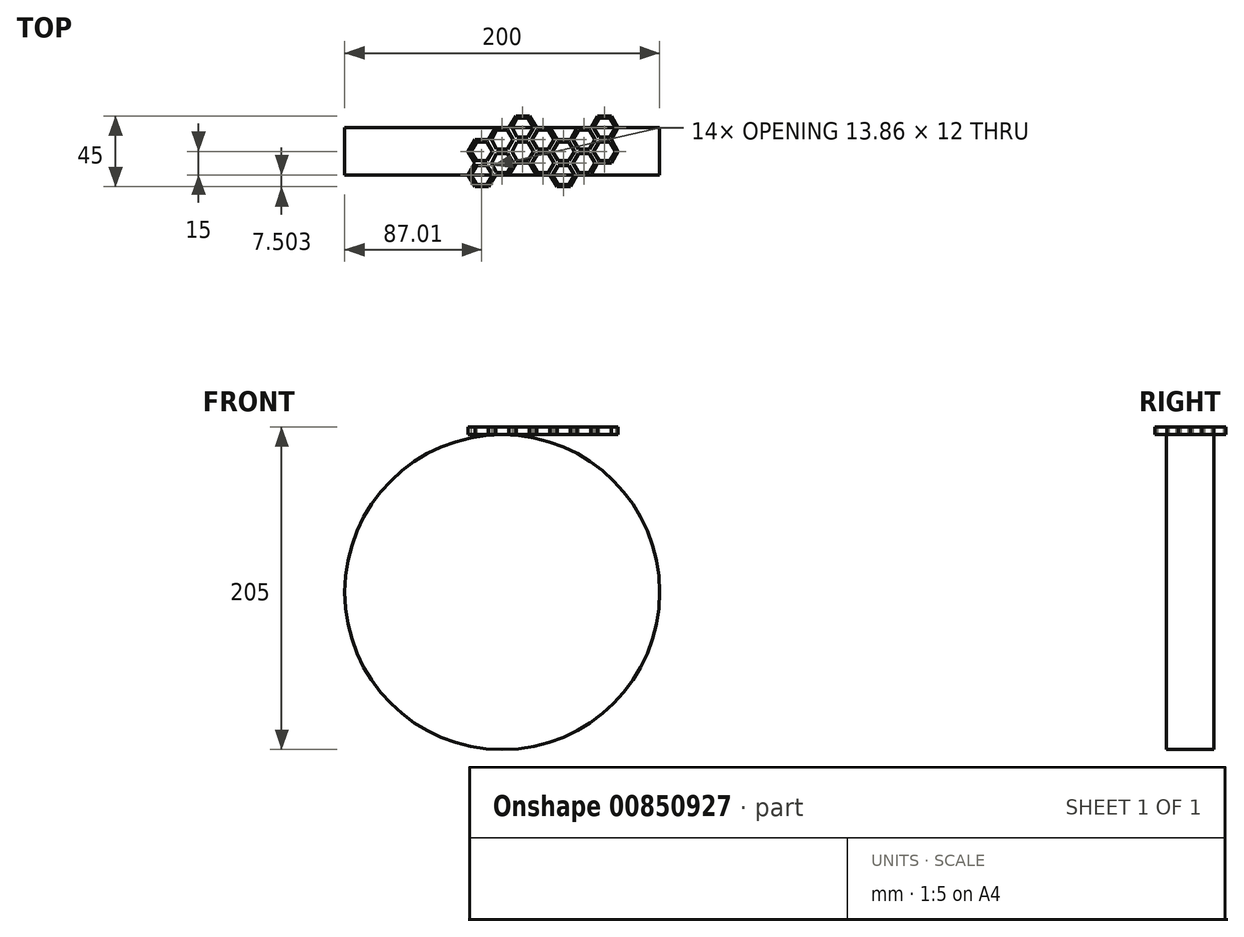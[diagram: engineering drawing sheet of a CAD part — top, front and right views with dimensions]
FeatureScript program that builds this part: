
annotation { "Feature Type Name" : "Feature", "Feature Type Description" : "" }
export const myFeature = defineFeature(function(context is Context, id is Id, definition is map)
    precondition{}
    {
        {
            var Q0;
            Q0=qCreatedBy(makeId("Front.planeOp"),FACE);
            var sketch = newSketch(context, id + "F0", { "sketchPlane" : qUnion([Q0])});
            skCircle(sketch, "E0", {"center": v(0, 0) * mm, "radius": 100 * mm});
            skSolve(sketch);
        }
        {
            var Q0;
            Q0=makeQuery(id+"F0.imprint","IMPRINT",FACE,{"disambiguationData":[TD([[makeQuery(id+"F0.imprint","IMPRINT",EDGE,{"derivedFrom":sQuery(id+"F0.wireOp",EDGE,"E0")}),1.0]])]});
            extrude(context, id + "F1", {"entities" : qUnion([Q0]), "depth" : 30 * mm, "offsetDistance" : 25 * mm});
        }
        {
            var Q0;
            Q0=qCreatedBy(makeId("Top.planeOp"),FACE);
            cPlane(context, id + "F2", {"entities" : qUnion([Q0]), "cplaneType" : CPlaneType.OFFSET, "offset" : 100 * mm, "width" : 150 * mm, "height" : 150 * mm});
        }
        {
            var Q0;
            Q0=qCreatedBy(id+"F2.planeOp",FACE);
            var sketch = newSketch(context, id + "F3", { "sketchPlane" : qUnion([Q0])});
            skCircle(sketch, "E1.cCircle", {"center": v(0, -7.45) * mm, "radius": 7.5 * mm, "construction": true});
            skLineSegment(sketch, "E1.0", {"start": v(4.33, -14.95) * mm, "end": v(-4.33, -14.95) * mm});
            skLineSegment(sketch, "E1.1", {"start": v(-4.33, -14.95) * mm, "end": v(-8.66, -7.45) * mm});
            skLineSegment(sketch, "E1.2", {"start": v(-8.66, -7.45) * mm, "end": v(-4.33, 0.05) * mm});
            skLineSegment(sketch, "E1.3", {"start": v(-4.33, 0.05) * mm, "end": v(4.33, 0.05) * mm});
            skLineSegment(sketch, "E1.4", {"start": v(4.33, 0.05) * mm, "end": v(8.66, -7.45) * mm});
            skLineSegment(sketch, "E1.5", {"start": v(8.66, -7.45) * mm, "end": v(4.33, -14.95) * mm});
            skPoint(sketch, "E1.0.midPoint", {"position": v(0, -14.95) * mm});
            skCircle(sketch, "E2.cCircle", {"center": v(0, -7.45) * mm, "radius": 6 * mm, "construction": true});
            skLineSegment(sketch, "E2.0", {"start": v(3.46, -13.45) * mm, "end": v(-3.46, -13.45) * mm});
            skLineSegment(sketch, "E2.1", {"start": v(-3.46, -13.45) * mm, "end": v(-6.93, -7.45) * mm});
            skLineSegment(sketch, "E2.2", {"start": v(-6.93, -7.45) * mm, "end": v(-3.46, -1.45) * mm});
            skLineSegment(sketch, "E2.3", {"start": v(-3.46, -1.45) * mm, "end": v(3.46, -1.45) * mm});
            skLineSegment(sketch, "E2.4", {"start": v(3.46, -1.45) * mm, "end": v(6.93, -7.45) * mm});
            skLineSegment(sketch, "E2.5", {"start": v(6.93, -7.45) * mm, "end": v(3.46, -13.45) * mm});
            skPoint(sketch, "E2.0.midPoint", {"position": v(0, -13.45) * mm});
            skCircle(sketch, "E3.cCircle", {"center": v(0, -22.45) * mm, "radius": 7.5 * mm, "construction": true});
            skLineSegment(sketch, "E3.0", {"start": v(4.33, -29.95) * mm, "end": v(-4.33, -29.95) * mm});
            skLineSegment(sketch, "E3.1", {"start": v(-4.33, -29.95) * mm, "end": v(-8.66, -22.45) * mm});
            skLineSegment(sketch, "E3.2", {"start": v(-8.66, -22.45) * mm, "end": v(-4.33, -14.95) * mm});
            skLineSegment(sketch, "E3.3", {"start": v(-4.33, -14.95) * mm, "end": v(4.33, -14.95) * mm});
            skLineSegment(sketch, "E3.4", {"start": v(4.33, -14.95) * mm, "end": v(8.66, -22.45) * mm});
            skLineSegment(sketch, "E3.5", {"start": v(8.66, -22.45) * mm, "end": v(4.33, -29.95) * mm});
            skPoint(sketch, "E3.0.midPoint", {"position": v(0, -29.95) * mm});
            skCircle(sketch, "E4.cCircle", {"center": v(0, -22.45) * mm, "radius": 6 * mm, "construction": true});
            skLineSegment(sketch, "E4.0", {"start": v(3.46, -28.45) * mm, "end": v(-3.46, -28.45) * mm});
            skLineSegment(sketch, "E4.1", {"start": v(-3.46, -28.45) * mm, "end": v(-6.93, -22.45) * mm});
            skLineSegment(sketch, "E4.2", {"start": v(-6.93, -22.45) * mm, "end": v(-3.46, -16.45) * mm});
            skLineSegment(sketch, "E4.3", {"start": v(-3.46, -16.45) * mm, "end": v(3.46, -16.45) * mm});
            skLineSegment(sketch, "E4.4", {"start": v(3.46, -16.45) * mm, "end": v(6.93, -22.45) * mm});
            skLineSegment(sketch, "E4.5", {"start": v(6.93, -22.45) * mm, "end": v(3.46, -28.45) * mm});
            skPoint(sketch, "E4.0.midPoint", {"position": v(0, -28.45) * mm});
            skCircle(sketch, "E5.cCircle", {"center": v(13, -14.95) * mm, "radius": 7.5 * mm, "construction": true});
            skLineSegment(sketch, "E5.0", {"start": v(17.32, -22.45) * mm, "end": v(8.66, -22.45) * mm});
            skLineSegment(sketch, "E5.1", {"start": v(8.66, -22.45) * mm, "end": v(4.33, -14.95) * mm});
            skLineSegment(sketch, "E5.2", {"start": v(4.33, -14.95) * mm, "end": v(8.66, -7.45) * mm});
            skLineSegment(sketch, "E5.3", {"start": v(8.66, -7.45) * mm, "end": v(17.32, -7.45) * mm});
            skLineSegment(sketch, "E5.4", {"start": v(17.32, -7.45) * mm, "end": v(21.65, -14.95) * mm});
            skLineSegment(sketch, "E5.5", {"start": v(21.65, -14.95) * mm, "end": v(17.32, -22.45) * mm});
            skPoint(sketch, "E5.0.midPoint", {"position": v(13, -22.45) * mm});
            skCircle(sketch, "E6.cCircle", {"center": v(13, -14.95) * mm, "radius": 6 * mm, "construction": true});
            skLineSegment(sketch, "E6.0", {"start": v(16.45, -20.95) * mm, "end": v(9.53, -20.95) * mm});
            skLineSegment(sketch, "E6.1", {"start": v(9.53, -20.95) * mm, "end": v(6.06, -14.95) * mm});
            skLineSegment(sketch, "E6.2", {"start": v(6.06, -14.95) * mm, "end": v(9.53, -8.95) * mm});
            skLineSegment(sketch, "E6.3", {"start": v(9.53, -8.95) * mm, "end": v(16.45, -8.95) * mm});
            skLineSegment(sketch, "E6.4", {"start": v(16.45, -8.95) * mm, "end": v(19.92, -14.95) * mm});
            skLineSegment(sketch, "E6.5", {"start": v(19.92, -14.95) * mm, "end": v(16.45, -20.95) * mm});
            skPoint(sketch, "E6.0.midPoint", {"position": v(13, -20.95) * mm});
            skCircle(sketch, "E7.cCircle", {"center": v(13, 0.05) * mm, "radius": 7.5 * mm, "construction": true});
            skLineSegment(sketch, "E7.0", {"start": v(17.32, -7.45) * mm, "end": v(8.66, -7.45) * mm});
            skLineSegment(sketch, "E7.1", {"start": v(8.66, -7.45) * mm, "end": v(4.33, 0.05) * mm});
            skLineSegment(sketch, "E7.2", {"start": v(4.33, 0.05) * mm, "end": v(8.66, 7.55) * mm});
            skLineSegment(sketch, "E7.3", {"start": v(8.66, 7.55) * mm, "end": v(17.32, 7.55) * mm});
            skLineSegment(sketch, "E7.4", {"start": v(17.32, 7.55) * mm, "end": v(21.65, 0.05) * mm});
            skLineSegment(sketch, "E7.5", {"start": v(21.65, 0.05) * mm, "end": v(17.32, -7.45) * mm});
            skPoint(sketch, "E7.0.midPoint", {"position": v(13, -7.45) * mm});
            skCircle(sketch, "E8.cCircle", {"center": v(13, 0.05) * mm, "radius": 6 * mm, "construction": true});
            skLineSegment(sketch, "E8.0", {"start": v(16.45, -5.95) * mm, "end": v(9.53, -5.95) * mm});
            skLineSegment(sketch, "E8.1", {"start": v(9.53, -5.95) * mm, "end": v(6.06, 0.05) * mm});
            skLineSegment(sketch, "E8.2", {"start": v(6.06, 0.05) * mm, "end": v(9.53, 6.05) * mm});
            skLineSegment(sketch, "E8.3", {"start": v(9.53, 6.05) * mm, "end": v(16.45, 6.05) * mm});
            skLineSegment(sketch, "E8.4", {"start": v(16.45, 6.05) * mm, "end": v(19.92, 0.05) * mm});
            skLineSegment(sketch, "E8.5", {"start": v(19.92, 0.05) * mm, "end": v(16.45, -5.95) * mm});
            skPoint(sketch, "E8.0.midPoint", {"position": v(13, -5.95) * mm});
            skCircle(sketch, "E9.cCircle", {"center": v(25.98, -7.45) * mm, "radius": 7.5 * mm, "construction": true});
            skLineSegment(sketch, "E9.0", {"start": v(30.31, -14.95) * mm, "end": v(21.65, -14.95) * mm});
            skLineSegment(sketch, "E9.1", {"start": v(21.65, -14.95) * mm, "end": v(17.32, -7.45) * mm});
            skLineSegment(sketch, "E9.2", {"start": v(17.32, -7.45) * mm, "end": v(21.65, 0.05) * mm});
            skLineSegment(sketch, "E9.3", {"start": v(21.65, 0.05) * mm, "end": v(30.31, 0.05) * mm});
            skLineSegment(sketch, "E9.4", {"start": v(30.31, 0.05) * mm, "end": v(34.64, -7.45) * mm});
            skLineSegment(sketch, "E9.5", {"start": v(34.64, -7.45) * mm, "end": v(30.31, -14.95) * mm});
            skPoint(sketch, "E9.0.midPoint", {"position": v(25.98, -14.95) * mm});
            skCircle(sketch, "E10.cCircle", {"center": v(25.98, -7.45) * mm, "radius": 6 * mm, "construction": true});
            skLineSegment(sketch, "E10.0", {"start": v(29.44, -13.45) * mm, "end": v(22.52, -13.45) * mm});
            skLineSegment(sketch, "E10.1", {"start": v(22.52, -13.45) * mm, "end": v(19.05, -7.45) * mm});
            skLineSegment(sketch, "E10.2", {"start": v(19.05, -7.45) * mm, "end": v(22.52, -1.45) * mm});
            skLineSegment(sketch, "E10.3", {"start": v(22.52, -1.45) * mm, "end": v(29.44, -1.45) * mm});
            skLineSegment(sketch, "E10.4", {"start": v(29.44, -1.45) * mm, "end": v(32.9, -7.45) * mm});
            skLineSegment(sketch, "E10.5", {"start": v(32.9, -7.45) * mm, "end": v(29.44, -13.45) * mm});
            skPoint(sketch, "E10.0.midPoint", {"position": v(25.98, -13.45) * mm});
            skCircle(sketch, "E11.cCircle", {"center": v(25.98, -22.45) * mm, "radius": 7.5 * mm, "construction": true});
            skLineSegment(sketch, "E11.0", {"start": v(30.31, -29.95) * mm, "end": v(21.65, -29.95) * mm});
            skLineSegment(sketch, "E11.1", {"start": v(21.65, -29.95) * mm, "end": v(17.32, -22.45) * mm});
            skLineSegment(sketch, "E11.2", {"start": v(17.32, -22.45) * mm, "end": v(21.65, -14.95) * mm});
            skLineSegment(sketch, "E11.3", {"start": v(21.65, -14.95) * mm, "end": v(30.31, -14.95) * mm});
            skLineSegment(sketch, "E11.4", {"start": v(30.31, -14.95) * mm, "end": v(34.64, -22.45) * mm});
            skLineSegment(sketch, "E11.5", {"start": v(34.64, -22.45) * mm, "end": v(30.31, -29.95) * mm});
            skPoint(sketch, "E11.0.midPoint", {"position": v(25.98, -29.95) * mm});
            skCircle(sketch, "E12.cCircle", {"center": v(25.98, -22.45) * mm, "radius": 6 * mm, "construction": true});
            skLineSegment(sketch, "E12.0", {"start": v(29.44, -28.45) * mm, "end": v(22.52, -28.45) * mm});
            skLineSegment(sketch, "E12.1", {"start": v(22.52, -28.45) * mm, "end": v(19.05, -22.45) * mm});
            skLineSegment(sketch, "E12.2", {"start": v(19.05, -22.45) * mm, "end": v(22.52, -16.45) * mm});
            skLineSegment(sketch, "E12.3", {"start": v(22.52, -16.45) * mm, "end": v(29.44, -16.45) * mm});
            skLineSegment(sketch, "E12.4", {"start": v(29.44, -16.45) * mm, "end": v(32.9, -22.45) * mm});
            skLineSegment(sketch, "E12.5", {"start": v(32.9, -22.45) * mm, "end": v(29.44, -28.45) * mm});
            skPoint(sketch, "E12.0.midPoint", {"position": v(25.98, -28.45) * mm});
            skCircle(sketch, "E13.cCircle", {"center": v(38.97, -29.95) * mm, "radius": 7.5 * mm, "construction": true});
            skLineSegment(sketch, "E13.0", {"start": v(43.3, -37.45) * mm, "end": v(34.64, -37.45) * mm});
            skLineSegment(sketch, "E13.1", {"start": v(34.64, -37.45) * mm, "end": v(30.31, -29.95) * mm});
            skLineSegment(sketch, "E13.2", {"start": v(30.31, -29.95) * mm, "end": v(34.64, -22.45) * mm});
            skLineSegment(sketch, "E13.3", {"start": v(34.64, -22.45) * mm, "end": v(43.3, -22.45) * mm});
            skLineSegment(sketch, "E13.4", {"start": v(43.3, -22.45) * mm, "end": v(47.63, -29.95) * mm});
            skLineSegment(sketch, "E13.5", {"start": v(47.63, -29.95) * mm, "end": v(43.3, -37.45) * mm});
            skPoint(sketch, "E13.0.midPoint", {"position": v(38.97, -37.45) * mm});
            skCircle(sketch, "E14.cCircle", {"center": v(38.97, -29.95) * mm, "radius": 6 * mm, "construction": true});
            skLineSegment(sketch, "E14.0", {"start": v(42.44, -35.95) * mm, "end": v(35.5, -35.95) * mm});
            skLineSegment(sketch, "E14.1", {"start": v(35.5, -35.95) * mm, "end": v(32.04, -29.95) * mm});
            skLineSegment(sketch, "E14.2", {"start": v(32.04, -29.95) * mm, "end": v(35.5, -23.95) * mm});
            skLineSegment(sketch, "E14.3", {"start": v(35.5, -23.95) * mm, "end": v(42.44, -23.95) * mm});
            skLineSegment(sketch, "E14.4", {"start": v(42.44, -23.95) * mm, "end": v(45.9, -29.95) * mm});
            skLineSegment(sketch, "E14.5", {"start": v(45.9, -29.95) * mm, "end": v(42.44, -35.95) * mm});
            skPoint(sketch, "E14.0.midPoint", {"position": v(38.97, -35.95) * mm});
            skCircle(sketch, "E15.cCircle", {"center": v(38.97, -14.95) * mm, "radius": 7.5 * mm, "construction": true});
            skLineSegment(sketch, "E15.0", {"start": v(43.3, -22.45) * mm, "end": v(34.64, -22.45) * mm});
            skLineSegment(sketch, "E15.1", {"start": v(34.64, -22.45) * mm, "end": v(30.31, -14.95) * mm});
            skLineSegment(sketch, "E15.2", {"start": v(30.31, -14.95) * mm, "end": v(34.64, -7.45) * mm});
            skLineSegment(sketch, "E15.3", {"start": v(34.64, -7.45) * mm, "end": v(43.3, -7.45) * mm});
            skLineSegment(sketch, "E15.4", {"start": v(43.3, -7.45) * mm, "end": v(47.63, -14.95) * mm});
            skLineSegment(sketch, "E15.5", {"start": v(47.63, -14.95) * mm, "end": v(43.3, -22.45) * mm});
            skPoint(sketch, "E15.0.midPoint", {"position": v(38.97, -22.45) * mm});
            skCircle(sketch, "E16.cCircle", {"center": v(38.97, -14.95) * mm, "radius": 6 * mm, "construction": true});
            skLineSegment(sketch, "E16.0", {"start": v(42.44, -20.95) * mm, "end": v(35.5, -20.95) * mm});
            skLineSegment(sketch, "E16.1", {"start": v(35.5, -20.95) * mm, "end": v(32.04, -14.95) * mm});
            skLineSegment(sketch, "E16.2", {"start": v(32.04, -14.95) * mm, "end": v(35.5, -8.95) * mm});
            skLineSegment(sketch, "E16.3", {"start": v(35.5, -8.95) * mm, "end": v(42.44, -8.95) * mm});
            skLineSegment(sketch, "E16.4", {"start": v(42.44, -8.95) * mm, "end": v(45.9, -14.95) * mm});
            skLineSegment(sketch, "E16.5", {"start": v(45.9, -14.95) * mm, "end": v(42.44, -20.95) * mm});
            skPoint(sketch, "E16.0.midPoint", {"position": v(38.97, -20.95) * mm});
            skCircle(sketch, "E17.cCircle", {"center": v(51.96, -22.45) * mm, "radius": 7.5 * mm, "construction": true});
            skLineSegment(sketch, "E17.0", {"start": v(56.3, -29.95) * mm, "end": v(47.63, -29.95) * mm});
            skLineSegment(sketch, "E17.1", {"start": v(47.63, -29.95) * mm, "end": v(43.3, -22.45) * mm});
            skLineSegment(sketch, "E17.2", {"start": v(43.3, -22.45) * mm, "end": v(47.63, -14.95) * mm});
            skLineSegment(sketch, "E17.3", {"start": v(47.63, -14.95) * mm, "end": v(56.3, -14.95) * mm});
            skLineSegment(sketch, "E17.4", {"start": v(56.3, -14.95) * mm, "end": v(60.62, -22.45) * mm});
            skLineSegment(sketch, "E17.5", {"start": v(60.62, -22.45) * mm, "end": v(56.3, -29.95) * mm});
            skPoint(sketch, "E17.0.midPoint", {"position": v(51.96, -29.95) * mm});
            skCircle(sketch, "E18.cCircle", {"center": v(51.96, -22.45) * mm, "radius": 6 * mm, "construction": true});
            skLineSegment(sketch, "E18.0", {"start": v(55.43, -28.45) * mm, "end": v(48.5, -28.45) * mm});
            skLineSegment(sketch, "E18.1", {"start": v(48.5, -28.45) * mm, "end": v(45.03, -22.45) * mm});
            skLineSegment(sketch, "E18.2", {"start": v(45.03, -22.45) * mm, "end": v(48.5, -16.45) * mm});
            skLineSegment(sketch, "E18.3", {"start": v(48.5, -16.45) * mm, "end": v(55.43, -16.45) * mm});
            skLineSegment(sketch, "E18.4", {"start": v(55.43, -16.45) * mm, "end": v(58.89, -22.45) * mm});
            skLineSegment(sketch, "E18.5", {"start": v(58.89, -22.45) * mm, "end": v(55.43, -28.45) * mm});
            skPoint(sketch, "E18.0.midPoint", {"position": v(51.96, -28.45) * mm});
            skCircle(sketch, "E19.cCircle", {"center": v(51.96, -7.45) * mm, "radius": 7.5 * mm, "construction": true});
            skLineSegment(sketch, "E19.0", {"start": v(56.3, -14.95) * mm, "end": v(47.63, -14.95) * mm});
            skLineSegment(sketch, "E19.1", {"start": v(47.63, -14.95) * mm, "end": v(43.3, -7.45) * mm});
            skLineSegment(sketch, "E19.2", {"start": v(43.3, -7.45) * mm, "end": v(47.63, 0.05) * mm});
            skLineSegment(sketch, "E19.3", {"start": v(47.63, 0.05) * mm, "end": v(56.3, 0.05) * mm});
            skLineSegment(sketch, "E19.4", {"start": v(56.3, 0.05) * mm, "end": v(60.62, -7.45) * mm});
            skLineSegment(sketch, "E19.5", {"start": v(60.62, -7.45) * mm, "end": v(56.3, -14.95) * mm});
            skPoint(sketch, "E19.0.midPoint", {"position": v(51.96, -14.95) * mm});
            skCircle(sketch, "E20.cCircle", {"center": v(51.96, -7.45) * mm, "radius": 6 * mm, "construction": true});
            skLineSegment(sketch, "E20.0", {"start": v(55.43, -13.45) * mm, "end": v(48.5, -13.45) * mm});
            skLineSegment(sketch, "E20.1", {"start": v(48.5, -13.45) * mm, "end": v(45.03, -7.45) * mm});
            skLineSegment(sketch, "E20.2", {"start": v(45.03, -7.45) * mm, "end": v(48.5, -1.45) * mm});
            skLineSegment(sketch, "E20.3", {"start": v(48.5, -1.45) * mm, "end": v(55.43, -1.45) * mm});
            skLineSegment(sketch, "E20.4", {"start": v(55.43, -1.45) * mm, "end": v(58.89, -7.45) * mm});
            skLineSegment(sketch, "E20.5", {"start": v(58.89, -7.45) * mm, "end": v(55.43, -13.45) * mm});
            skPoint(sketch, "E20.0.midPoint", {"position": v(51.96, -13.45) * mm});
            skCircle(sketch, "E21.cCircle", {"center": v(64.95, -14.95) * mm, "radius": 7.5 * mm, "construction": true});
            skLineSegment(sketch, "E21.0", {"start": v(69.28, -22.45) * mm, "end": v(60.62, -22.45) * mm});
            skLineSegment(sketch, "E21.1", {"start": v(60.62, -22.45) * mm, "end": v(56.3, -14.95) * mm});
            skLineSegment(sketch, "E21.2", {"start": v(56.3, -14.95) * mm, "end": v(60.62, -7.45) * mm});
            skLineSegment(sketch, "E21.3", {"start": v(60.62, -7.45) * mm, "end": v(69.28, -7.45) * mm});
            skLineSegment(sketch, "E21.4", {"start": v(69.28, -7.45) * mm, "end": v(73.61, -14.95) * mm});
            skLineSegment(sketch, "E21.5", {"start": v(73.61, -14.95) * mm, "end": v(69.28, -22.45) * mm});
            skPoint(sketch, "E21.0.midPoint", {"position": v(64.95, -22.45) * mm});
            skCircle(sketch, "E22.cCircle", {"center": v(64.95, -14.95) * mm, "radius": 6 * mm, "construction": true});
            skLineSegment(sketch, "E22.0", {"start": v(68.42, -20.95) * mm, "end": v(61.49, -20.95) * mm});
            skLineSegment(sketch, "E22.1", {"start": v(61.49, -20.95) * mm, "end": v(58.02, -14.95) * mm});
            skLineSegment(sketch, "E22.2", {"start": v(58.02, -14.95) * mm, "end": v(61.49, -8.95) * mm});
            skLineSegment(sketch, "E22.3", {"start": v(61.49, -8.95) * mm, "end": v(68.42, -8.95) * mm});
            skLineSegment(sketch, "E22.4", {"start": v(68.42, -8.95) * mm, "end": v(71.88, -14.95) * mm});
            skLineSegment(sketch, "E22.5", {"start": v(71.88, -14.95) * mm, "end": v(68.42, -20.95) * mm});
            skPoint(sketch, "E22.0.midPoint", {"position": v(64.95, -20.95) * mm});
            skCircle(sketch, "E23.cCircle", {"center": v(64.95, 0.05) * mm, "radius": 7.5 * mm, "construction": true});
            skLineSegment(sketch, "E23.0", {"start": v(69.28, -7.45) * mm, "end": v(60.62, -7.45) * mm});
            skLineSegment(sketch, "E23.1", {"start": v(60.62, -7.45) * mm, "end": v(56.3, 0.05) * mm});
            skLineSegment(sketch, "E23.2", {"start": v(56.3, 0.05) * mm, "end": v(60.62, 7.55) * mm});
            skLineSegment(sketch, "E23.3", {"start": v(60.62, 7.55) * mm, "end": v(69.28, 7.55) * mm});
            skLineSegment(sketch, "E23.4", {"start": v(69.28, 7.55) * mm, "end": v(73.61, 0.05) * mm});
            skLineSegment(sketch, "E23.5", {"start": v(73.61, 0.05) * mm, "end": v(69.28, -7.45) * mm});
            skPoint(sketch, "E23.0.midPoint", {"position": v(64.95, -7.45) * mm});
            skCircle(sketch, "E24.cCircle", {"center": v(64.95, 0.05) * mm, "radius": 6 * mm, "construction": true});
            skLineSegment(sketch, "E24.0", {"start": v(68.42, -5.95) * mm, "end": v(61.49, -5.95) * mm});
            skLineSegment(sketch, "E24.1", {"start": v(61.49, -5.95) * mm, "end": v(58.02, 0.05) * mm});
            skLineSegment(sketch, "E24.2", {"start": v(58.02, 0.05) * mm, "end": v(61.49, 6.05) * mm});
            skLineSegment(sketch, "E24.3", {"start": v(61.49, 6.05) * mm, "end": v(68.42, 6.05) * mm});
            skLineSegment(sketch, "E24.4", {"start": v(68.42, 6.05) * mm, "end": v(71.88, 0.05) * mm});
            skLineSegment(sketch, "E24.5", {"start": v(71.88, 0.05) * mm, "end": v(68.42, -5.95) * mm});
            skPoint(sketch, "E24.0.midPoint", {"position": v(64.95, -5.95) * mm});
            skCircle(sketch, "E25.cCircle", {"center": v(-13, -14.95) * mm, "radius": 7.5 * mm, "construction": true});
            skLineSegment(sketch, "E25.0", {"start": v(-8.66, -22.45) * mm, "end": v(-17.32, -22.45) * mm});
            skLineSegment(sketch, "E25.1", {"start": v(-17.32, -22.45) * mm, "end": v(-21.65, -14.95) * mm});
            skLineSegment(sketch, "E25.2", {"start": v(-21.65, -14.95) * mm, "end": v(-17.32, -7.45) * mm});
            skLineSegment(sketch, "E25.3", {"start": v(-17.32, -7.45) * mm, "end": v(-8.66, -7.45) * mm});
            skLineSegment(sketch, "E25.4", {"start": v(-8.66, -7.45) * mm, "end": v(-4.33, -14.95) * mm});
            skLineSegment(sketch, "E25.5", {"start": v(-4.33, -14.95) * mm, "end": v(-8.66, -22.45) * mm});
            skPoint(sketch, "E25.0.midPoint", {"position": v(-13, -22.45) * mm});
            skCircle(sketch, "E26.cCircle", {"center": v(-13, -14.95) * mm, "radius": 6 * mm, "construction": true});
            skLineSegment(sketch, "E26.0", {"start": v(-9.53, -20.95) * mm, "end": v(-16.45, -20.95) * mm});
            skLineSegment(sketch, "E26.1", {"start": v(-16.45, -20.95) * mm, "end": v(-19.92, -14.95) * mm});
            skLineSegment(sketch, "E26.2", {"start": v(-19.92, -14.95) * mm, "end": v(-16.45, -8.95) * mm});
            skLineSegment(sketch, "E26.3", {"start": v(-16.45, -8.95) * mm, "end": v(-9.53, -8.95) * mm});
            skLineSegment(sketch, "E26.4", {"start": v(-9.53, -8.95) * mm, "end": v(-6.06, -14.95) * mm});
            skLineSegment(sketch, "E26.5", {"start": v(-6.06, -14.95) * mm, "end": v(-9.53, -20.95) * mm});
            skPoint(sketch, "E26.0.midPoint", {"position": v(-13, -20.95) * mm});
            skCircle(sketch, "E27.cCircle", {"center": v(-13, -29.95) * mm, "radius": 7.5 * mm, "construction": true});
            skLineSegment(sketch, "E27.0", {"start": v(-8.66, -37.45) * mm, "end": v(-17.32, -37.45) * mm});
            skLineSegment(sketch, "E27.1", {"start": v(-17.32, -37.45) * mm, "end": v(-21.65, -29.95) * mm});
            skLineSegment(sketch, "E27.2", {"start": v(-21.65, -29.95) * mm, "end": v(-17.32, -22.45) * mm});
            skLineSegment(sketch, "E27.3", {"start": v(-17.32, -22.45) * mm, "end": v(-8.66, -22.45) * mm});
            skLineSegment(sketch, "E27.4", {"start": v(-8.66, -22.45) * mm, "end": v(-4.33, -29.95) * mm});
            skLineSegment(sketch, "E27.5", {"start": v(-4.33, -29.95) * mm, "end": v(-8.66, -37.45) * mm});
            skPoint(sketch, "E27.0.midPoint", {"position": v(-13, -37.45) * mm});
            skCircle(sketch, "E28.cCircle", {"center": v(-13, -29.95) * mm, "radius": 6 * mm, "construction": true});
            skLineSegment(sketch, "E28.0", {"start": v(-9.53, -35.95) * mm, "end": v(-16.45, -35.95) * mm});
            skLineSegment(sketch, "E28.1", {"start": v(-16.45, -35.95) * mm, "end": v(-19.92, -29.95) * mm});
            skLineSegment(sketch, "E28.2", {"start": v(-19.92, -29.95) * mm, "end": v(-16.45, -23.95) * mm});
            skLineSegment(sketch, "E28.3", {"start": v(-16.45, -23.95) * mm, "end": v(-9.53, -23.95) * mm});
            skLineSegment(sketch, "E28.4", {"start": v(-9.53, -23.95) * mm, "end": v(-6.06, -29.95) * mm});
            skLineSegment(sketch, "E28.5", {"start": v(-6.06, -29.95) * mm, "end": v(-9.53, -35.95) * mm});
            skPoint(sketch, "E28.0.midPoint", {"position": v(-13, -35.95) * mm});
            skSolve(sketch);
        }
        {
            var Q0;
            Q0 = qSketchRegion(id + "F3", true);
            extrude(context, id + "F4", {"entities" : qUnion([Q0]), "operationType" : NewBodyOperationType.ADD, "depth" : 5 * mm, "offsetDistance" : 25 * mm});
        }
    });
